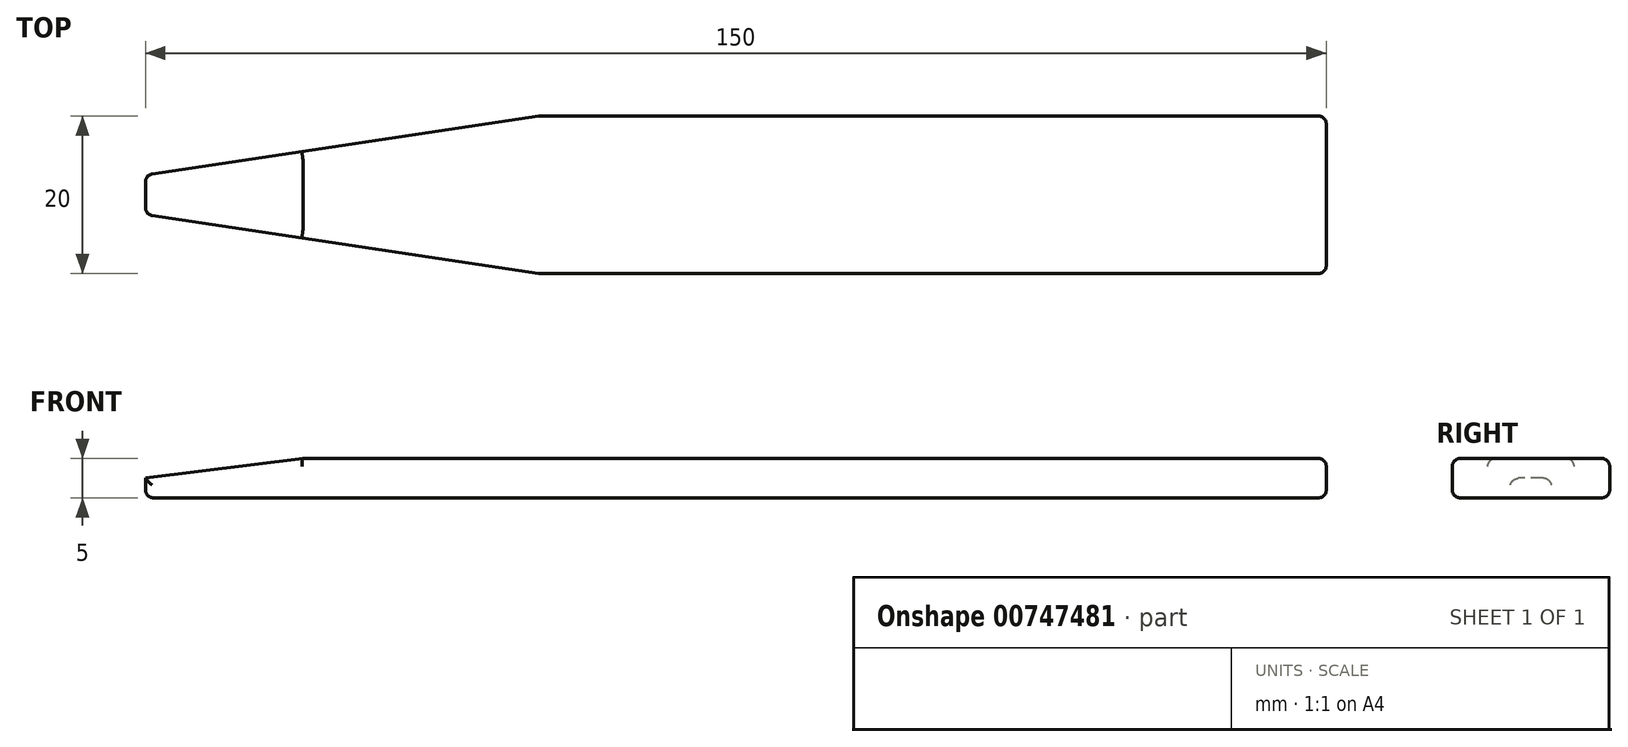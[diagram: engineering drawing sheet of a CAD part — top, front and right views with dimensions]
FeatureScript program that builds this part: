
annotation { "Feature Type Name" : "Feature", "Feature Type Description" : "" }
export const myFeature = defineFeature(function(context is Context, id is Id, definition is map)
    precondition{}
    {
        {
            var Q0;
            Q0=qCreatedBy(makeId("Top.planeOp"),FACE);
            var sketch = newSketch(context, id + "F0", { "sketchPlane" : qUnion([Q0])});
            skLineSegment(sketch, "E0.bottom", {"start": v(-100, 20) * mm, "end": v(0, 20) * mm});
            skLineSegment(sketch, "E0.top", {"start": v(-100, 0) * mm, "end": v(0, 0) * mm});
            skLineSegment(sketch, "E0.left", {"start": v(-150, 12.5) * mm, "end": v(-150, 7.5) * mm});
            skLineSegment(sketch, "E0.right", {"start": v(0, 20) * mm, "end": v(0, 0) * mm});
            skLineSegment(sketch, "E1", {"start": v(-150, 12.5) * mm, "end": v(-100, 20) * mm});
            skLineSegment(sketch, "E2", {"start": v(-150, 7.5) * mm, "end": v(-100, 0) * mm});
            skLineSegment(sketch, "E3", {"start": v(-100, 31.93) * mm, "end": v(-100, -21.04) * mm, "construction": true});
            skPoint(sketch, "E4.orphan", {"position": v(-150, 20) * mm});
            skSolve(sketch);
        }
        {
            var Q0;
            Q0=makeQuery(id+"F0.imprint","IMPRINT",FACE,{"disambiguationData":[TD([[makeQuery(id+"F0.imprint","IMPRINT",EDGE,{"derivedFrom":sQuery(id+"F0.wireOp",EDGE,"E0.bottom")}),-1.0]])]});
            extrude(context, id + "F1", {"entities" : qUnion([Q0]), "depth" : 5 * mm, "offsetDistance" : 25 * mm});
        }
        {
            var Q0;
            Q0=makeQuery(id+"F1.opExtrude","SWEPT_FACE",FACE,{"disambiguationData":[OSD([sQuery(id+"F0.wireOp",EDGE,"E0.top")])]});
            var sketch = newSketch(context, id + "F2", { "sketchPlane" : qUnion([Q0])});
            skLineSegment(sketch, "E5", {"start": v(-150, 2.5) * mm, "end": v(-130, 5) * mm});
            skLineSegment(sketch, "E6", {"start": v(-130, 5) * mm, "end": v(-150, 5) * mm});
            skLineSegment(sketch, "E7", {"start": v(-150, 5) * mm, "end": v(-150, 2.5) * mm});
            skSolve(sketch);
        }
        {
            var Q0;
            Q0=makeQuery(id+"F2.imprint","IMPRINT",FACE,{"disambiguationData":[TD([[makeQuery(id+"F2.imprint","IMPRINT",EDGE,{"derivedFrom":sQuery(id+"F2.wireOp",EDGE,"E5")}),1.0]])]});
            extrude(context, id + "F3", {"entities" : qUnion([Q0]), "operationType" : NewBodyOperationType.REMOVE, "endBound" : BoundingType.THROUGH_ALL, "oppositeDirection" : true, "depth" : 25 * mm, "offsetDistance" : 25 * mm});
        }
        {
            var Q0;
            Q0=makeQuery(id+"F1.opExtrude","CAP_EDGE",EDGE,{"disambiguationData":[OSD([sQuery(id+"F0.wireOp",EDGE,"E2")])],"isStart":false});
            var Q1;
            Q1=makeQuery(id+"F3.boolean.opBoolean","INTERSECT",EDGE,{"derivedFrom":[makeQuery(id+"F1.opExtrude","SWEPT_FACE",FACE,{"disambiguationData":[OSD([sQuery(id+"F0.wireOp",EDGE,"E2")])]}),makeQuery(id+"F3.opExtrude","SWEPT_FACE",FACE,{"disambiguationData":[OSD([sQuery(id+"F2.wireOp",EDGE,"E5")])]})]});
            var Q2;
            Q2=makeQuery(id+"F3.boolean.opBoolean","COPY",EDGE,{"derivedFrom":makeQuery(id+"F3.opExtrude","SWEPT_EDGE",EDGE,{"disambiguationData":[OSD([sQuery(id+"F2.wireOp",EDGE,"E5"),sQuery(id+"F2.wireOp",EDGE,"E7")])]})});
            var Q3;
            Q3=makeQuery(id+"F1.opExtrude","CAP_EDGE",EDGE,{"disambiguationData":[OSD([sQuery(id+"F0.wireOp",EDGE,"E0.left")])],"isStart":true});
            var Q4;
            Q4=makeQuery(id+"F1.opExtrude","SWEPT_EDGE",EDGE,{"disambiguationData":[OSD([sQuery(id+"F0.wireOp",EDGE,"E0.left"),sQuery(id+"F0.wireOp",EDGE,"E2")])]});
            var Q5;
            Q5=makeQuery(id+"F1.opExtrude","SWEPT_EDGE",EDGE,{"disambiguationData":[OSD([sQuery(id+"F0.wireOp",EDGE,"E0.left"),sQuery(id+"F0.wireOp",EDGE,"E1")])]});
            var Q6;
            Q6=makeQuery(id+"F3.boolean.opBoolean","INTERSECT",EDGE,{"derivedFrom":[makeQuery(id+"F1.opExtrude","SWEPT_FACE",FACE,{"disambiguationData":[OSD([sQuery(id+"F0.wireOp",EDGE,"E1")])]}),makeQuery(id+"F3.opExtrude","SWEPT_FACE",FACE,{"disambiguationData":[OSD([sQuery(id+"F2.wireOp",EDGE,"E5")])]})]});
            var Q7;
            Q7=makeQuery(id+"F1.opExtrude","CAP_EDGE",EDGE,{"disambiguationData":[OSD([sQuery(id+"F0.wireOp",EDGE,"E1")])],"isStart":false});
            var Q8;
            Q8=makeQuery(id+"F1.opExtrude","CAP_EDGE",EDGE,{"disambiguationData":[OSD([sQuery(id+"F0.wireOp",EDGE,"E1")])],"isStart":true});
            var Q9;
            Q9=makeQuery(id+"F3.boolean.opBoolean","COPY",EDGE,{"derivedFrom":makeQuery(id+"F3.opExtrude","SWEPT_EDGE",EDGE,{"disambiguationData":[OSD([sQuery(id+"F2.wireOp",EDGE,"E5"),sQuery(id+"F2.wireOp",EDGE,"E6")])]})});
            var Q10;
            Q10=makeQuery(id+"F1.opExtrude","CAP_EDGE",EDGE,{"disambiguationData":[OSD([sQuery(id+"F0.wireOp",EDGE,"E2")])],"isStart":true});
            var Q11;
            Q11=makeQuery(id+"F1.opExtrude","CAP_EDGE",EDGE,{"disambiguationData":[OSD([sQuery(id+"F0.wireOp",EDGE,"E0.top")])],"isStart":true});
            var Q12;
            Q12=makeQuery(id+"F1.opExtrude","CAP_EDGE",EDGE,{"disambiguationData":[OSD([sQuery(id+"F0.wireOp",EDGE,"E0.top")])],"isStart":false});
            var Q13;
            Q13=makeQuery(id+"F1.opExtrude","SWEPT_EDGE",EDGE,{"disambiguationData":[OSD([sQuery(id+"F0.wireOp",EDGE,"E0.top"),sQuery(id+"F0.wireOp",EDGE,"E2")])]});
            var Q14;
            Q14=makeQuery(id+"F1.opExtrude","SWEPT_EDGE",EDGE,{"disambiguationData":[OSD([sQuery(id+"F0.wireOp",EDGE,"E0.bottom"),sQuery(id+"F0.wireOp",EDGE,"E1")])]});
            var Q15;
            Q15=makeQuery(id+"F1.opExtrude","CAP_EDGE",EDGE,{"disambiguationData":[OSD([sQuery(id+"F0.wireOp",EDGE,"E0.bottom")])],"isStart":false});
            var Q16;
            Q16=makeQuery(id+"F1.opExtrude","CAP_EDGE",EDGE,{"disambiguationData":[OSD([sQuery(id+"F0.wireOp",EDGE,"E0.bottom")])],"isStart":true});
            var Q17;
            Q17=makeQuery(id+"F1.opExtrude","SWEPT_EDGE",EDGE,{"disambiguationData":[OSD([sQuery(id+"F0.wireOp",EDGE,"E0.bottom"),sQuery(id+"F0.wireOp",EDGE,"E0.right")])]});
            var Q18;
            Q18=makeQuery(id+"F1.opExtrude","SWEPT_EDGE",EDGE,{"disambiguationData":[OSD([sQuery(id+"F0.wireOp",EDGE,"E0.top"),sQuery(id+"F0.wireOp",EDGE,"E0.right")])]});
            var Q19;
            Q19=makeQuery(id+"F1.opExtrude","CAP_EDGE",EDGE,{"disambiguationData":[OSD([sQuery(id+"F0.wireOp",EDGE,"E0.right")])],"isStart":false});
            var Q20;
            Q20=makeQuery(id+"F1.opExtrude","CAP_EDGE",EDGE,{"disambiguationData":[OSD([sQuery(id+"F0.wireOp",EDGE,"E0.right")])],"isStart":true});
            fillet(context, id + "F4", {"entities" : qUnion([Q0, Q1, Q2, Q3, Q4, Q5, Q6, Q7, Q8, Q9, Q10, Q11, Q12, Q13, Q14, Q15, Q16, Q17, Q18, Q19, Q20]), "radius" : 1 * mm, "tangentPropagation" : true, "allowEdgeOverflow" : false});
        }
    });
